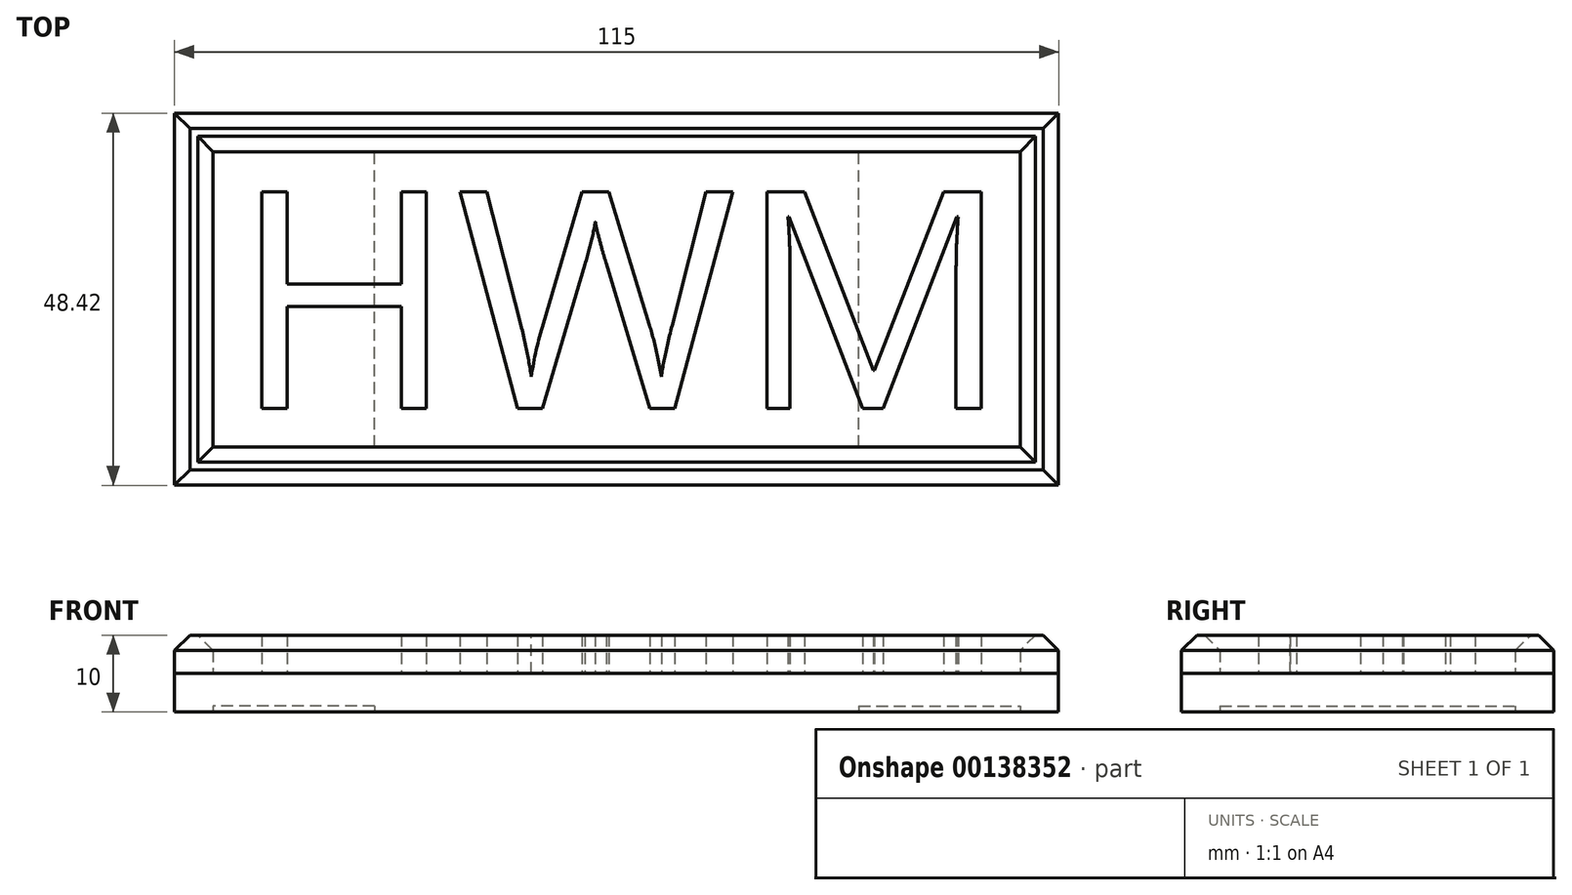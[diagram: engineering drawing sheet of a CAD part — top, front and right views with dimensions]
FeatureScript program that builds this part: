
annotation { "Feature Type Name" : "Feature", "Feature Type Description" : "" }
export const myFeature = defineFeature(function(context is Context, id is Id, definition is map)
    precondition{}
    {
        {
            var Q0;
            Q0=qCreatedBy(makeId("Top.planeOp"),FACE);
            var sketch = newSketch(context, id + "F0", { "sketchPlane" : qUnion([Q0])});
            skText(sketch, "E0", { "text": "HWM", "fontName": "OpenSans-Regular.ttf"});
            skPoint(sketch, "E1", {"position": v(-52.9, -24.96) * mm});
            skLineSegment(sketch, "E2.bottom", {"start": v(-0.4, -44.17) * mm, "end": v(-105.4, -44.17) * mm});
            skLineSegment(sketch, "E2.top", {"start": v(-0.4, -5.75) * mm, "end": v(-105.4, -5.75) * mm});
            skLineSegment(sketch, "E2.left", {"start": v(-0.4, -44.17) * mm, "end": v(-0.4, -5.75) * mm});
            skLineSegment(sketch, "E2.right", {"start": v(-105.4, -44.17) * mm, "end": v(-105.4, -5.75) * mm});
            skLineSegment(sketch, "E3.0", {"start": v(4.6, -0.75) * mm, "end": v(-110.4, -0.75) * mm});
            skLineSegment(sketch, "E3.1", {"start": v(4.6, -49.17) * mm, "end": v(4.6, -0.75) * mm});
            skLineSegment(sketch, "E3.2", {"start": v(4.6, -49.17) * mm, "end": v(-110.4, -49.17) * mm});
            skLineSegment(sketch, "E3.3", {"start": v(-110.4, -49.17) * mm, "end": v(-110.4, -0.75) * mm});
            const initialGuessF0  = {"E0": [-0.1029, -0.03917, 1, 0, 0.02842]};
            skSetInitialGuess(sketch, initialGuessF0);
            skSolve(sketch);
        }
        {
            var Q0;
            Q0=makeQuery(id+"F0.imprint","IMPRINT",FACE,{"disambiguationData":[TD([[makeQuery(id+"F0.imprint","IMPRINT",EDGE,{"derivedFrom":sQuery(id+"F0.wireOp",EDGE,"E0.sketch_text.stroke-0")}),-1.0]])]});
            var Q1;
            Q1=makeQuery(id+"F0.imprint","IMPRINT",FACE,{"disambiguationData":[TD([[makeQuery(id+"F0.imprint","IMPRINT",EDGE,{"derivedFrom":sQuery(id+"F0.wireOp",EDGE,"E0.sketch_text.stroke-12")}),-1.0]])]});
            var Q2;
            Q2=makeQuery(id+"F0.imprint","IMPRINT",FACE,{"disambiguationData":[TD([[makeQuery(id+"F0.imprint","IMPRINT",EDGE,{"derivedFrom":sQuery(id+"F0.wireOp",EDGE,"E0.sketch_text.stroke-32")}),-1.0]])]});
            var Q3;
            Q3=makeQuery(id+"F0.imprint","IMPRINT",FACE,{"disambiguationData":[TD([[makeQuery(id+"F0.imprint","IMPRINT",EDGE,{"derivedFrom":sQuery(id+"F0.wireOp",EDGE,"E2.bottom")}),1.0]])]});
            extrude(context, id + "F1", {"entities" : qUnion([Q0, Q1, Q2, Q3]), "depth" : 5 * mm});
        }
        {
            var Q0;
            Q0=makeQuery(id+"F0.imprint","IMPRINT",FACE,{"disambiguationData":[TD([[makeQuery(id+"F0.imprint","IMPRINT",EDGE,{"derivedFrom":sQuery(id+"F0.wireOp",EDGE,"E0.sketch_text.stroke-0")}),-1.0]])]});
            var Q1;
            Q1=makeQuery(id+"F0.imprint","IMPRINT",FACE,{"disambiguationData":[TD([[makeQuery(id+"F0.imprint","IMPRINT",EDGE,{"derivedFrom":sQuery(id+"F0.wireOp",EDGE,"E0.sketch_text.stroke-12")}),-1.0]])]});
            var Q2;
            Q2=makeQuery(id+"F0.imprint","IMPRINT",FACE,{"disambiguationData":[TD([[makeQuery(id+"F0.imprint","IMPRINT",EDGE,{"derivedFrom":sQuery(id+"F0.wireOp",EDGE,"E0.sketch_text.stroke-32")}),-1.0]])]});
            var Q3;
            Q3=makeQuery(id+"F0.imprint","IMPRINT",FACE,{"disambiguationData":[TD([[makeQuery(id+"F0.imprint","IMPRINT",EDGE,{"derivedFrom":sQuery(id+"F0.wireOp",EDGE,"E0.sketch_text.stroke-0")}),1.0]])]});
            var Q4;
            Q4=makeQuery(id+"F0.imprint","IMPRINT",FACE,{"disambiguationData":[TD([[makeQuery(id+"F0.imprint","IMPRINT",EDGE,{"derivedFrom":sQuery(id+"F0.wireOp",EDGE,"E2.bottom")}),1.0]])]});
            extrude(context, id + "F2", {"entities" : qUnion([Q0, Q1, Q2, Q3, Q4]), "oppositeDirection" : true, "depth" : 5 * mm});
        }
        {
            var Q0;
            Q0=makeQuery(id+"F1.opExtrude","CAP_EDGE",EDGE,{"disambiguationData":[OSD([sQuery(id+"F0.wireOp",EDGE,"E3.3")])],"isStart":false});
            var Q1;
            Q1=makeQuery(id+"F1.opExtrude","CAP_EDGE",EDGE,{"disambiguationData":[OSD([sQuery(id+"F0.wireOp",EDGE,"E3.0")])],"isStart":false});
            var Q2;
            Q2=makeQuery(id+"F1.opExtrude","CAP_EDGE",EDGE,{"disambiguationData":[OSD([sQuery(id+"F0.wireOp",EDGE,"E2.top")])],"isStart":false});
            var Q3;
            Q3=makeQuery(id+"F1.opExtrude","CAP_EDGE",EDGE,{"disambiguationData":[OSD([sQuery(id+"F0.wireOp",EDGE,"E2.right")])],"isStart":false});
            var Q4;
            Q4=makeQuery(id+"F1.opExtrude","CAP_EDGE",EDGE,{"disambiguationData":[OSD([sQuery(id+"F0.wireOp",EDGE,"E2.bottom")])],"isStart":false});
            var Q5;
            Q5=makeQuery(id+"F1.opExtrude","CAP_EDGE",EDGE,{"disambiguationData":[OSD([sQuery(id+"F0.wireOp",EDGE,"E3.2")])],"isStart":false});
            var Q6;
            Q6=makeQuery(id+"F1.opExtrude","CAP_EDGE",EDGE,{"disambiguationData":[OSD([sQuery(id+"F0.wireOp",EDGE,"E2.left")])],"isStart":false});
            var Q7;
            Q7=makeQuery(id+"F1.opExtrude","CAP_EDGE",EDGE,{"disambiguationData":[OSD([sQuery(id+"F0.wireOp",EDGE,"E3.1")])],"isStart":false});
            chamfer(context, id + "F3", {"entities" : qUnion([Q0, Q1, Q2, Q3, Q4, Q5, Q6, Q7]), "width" : 2 * mm, "tangentPropagation" : true});
        }
        {
            var Q0;
            Q0=makeQuery(id+"F2.opExtrude","CAP_FACE",FACE,{"disambiguationData":[OSD([sQuery(id+"F0.wireOp",EDGE,"E3.0"),sQuery(id+"F0.wireOp",EDGE,"E3.1"),sQuery(id+"F0.wireOp",EDGE,"E3.2"),sQuery(id+"F0.wireOp",EDGE,"E3.3")])],"isStart":false});
            var sketch = newSketch(context, id + "F4", { "sketchPlane" : qUnion([Q0])});
            skLineSegment(sketch, "E4.0.0", {"start": v(4.6, 0.75) * mm, "end": v(4.6, 49.17) * mm});
            skLineSegment(sketch, "E4.0.1", {"start": v(4.6, 49.17) * mm, "end": v(-110.4, 49.17) * mm});
            skLineSegment(sketch, "E4.0.2", {"start": v(-110.4, 49.17) * mm, "end": v(-110.4, 0.75) * mm});
            skLineSegment(sketch, "E4.0.3", {"start": v(-110.4, 0.75) * mm, "end": v(4.6, 0.75) * mm});
            skLineSegment(sketch, "E5.0", {"start": v(-0.4, 44.17) * mm, "end": v(-105.4, 44.17) * mm});
            skLineSegment(sketch, "E5.1", {"start": v(-0.4, 5.75) * mm, "end": v(-0.4, 44.17) * mm});
            skLineSegment(sketch, "E5.2", {"start": v(-105.4, 5.75) * mm, "end": v(-0.4, 5.75) * mm});
            skLineSegment(sketch, "E5.3", {"start": v(-105.4, 44.17) * mm, "end": v(-105.4, 5.75) * mm});
            skLineSegment(sketch, "E6", {"start": v(-84.4, 44.17) * mm, "end": v(-84.4, 5.75) * mm});
            skLineSegment(sketch, "E7", {"start": v(-21.4, 44.17) * mm, "end": v(-21.4, 5.75) * mm});
            skSolve(sketch);
        }
        {
            var Q0;
            {var subQ0=sQuery(id+"F4.wireOp",EDGE,"E5.3");Q0=makeQuery(id+"F4.imprint","IMPRINT",FACE,{"disambiguationData":[TD([[makeQuery(id+"F4.imprint","IMPRINT",EDGE,{"derivedFrom":subQ0}),1.0]])]});}
            var Q1;
            {var subQ0=sQuery(id+"F4.wireOp",EDGE,"E5.1");Q1=makeQuery(id+"F4.imprint","IMPRINT",FACE,{"disambiguationData":[TD([[makeQuery(id+"F4.imprint","IMPRINT",EDGE,{"derivedFrom":subQ0}),1.0]])]});}
            extrude(context, id + "F5", {"entities" : qUnion([Q0, Q1]), "operationType" : NewBodyOperationType.REMOVE, "oppositeDirection" : true, "depth" : .75 * mm});
        }
    });
